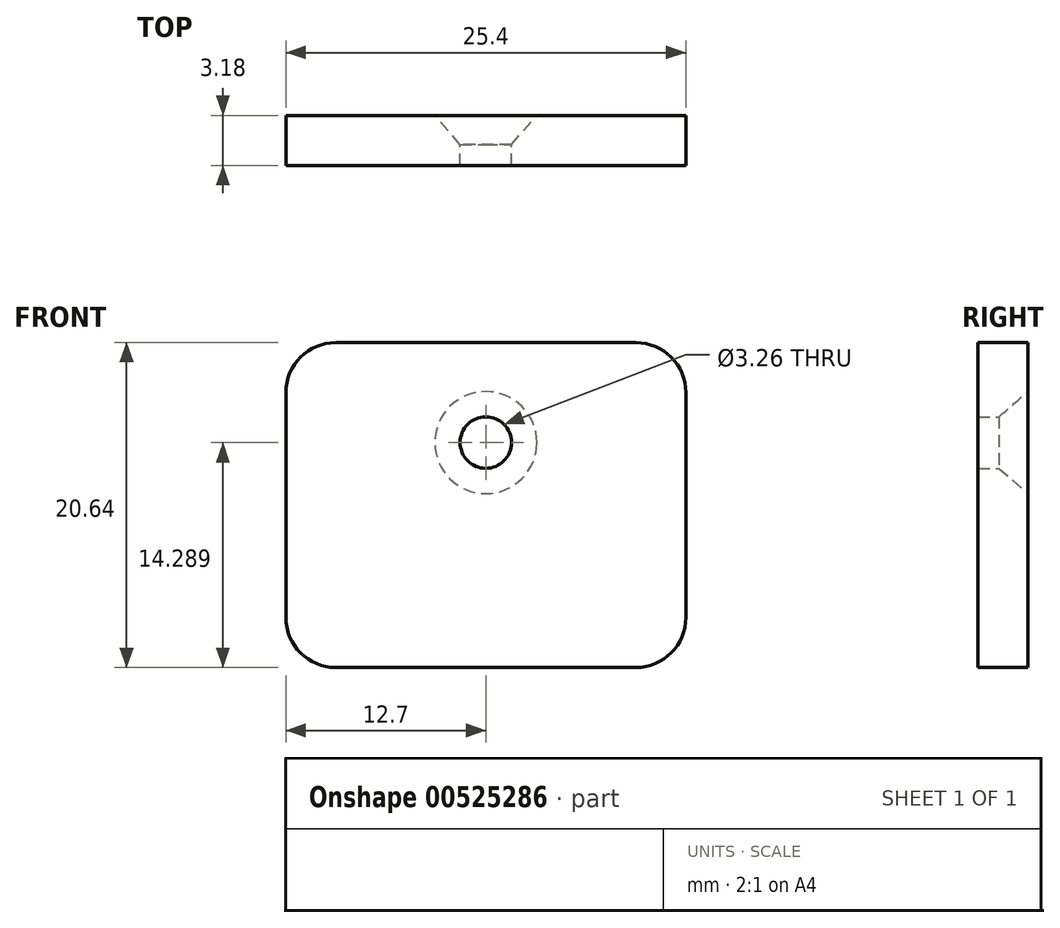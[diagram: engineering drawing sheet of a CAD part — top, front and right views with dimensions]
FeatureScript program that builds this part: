
annotation { "Feature Type Name" : "Feature", "Feature Type Description" : "" }
export const myFeature = defineFeature(function(context is Context, id is Id, definition is map)
    precondition{}
    {
        {
            var Q0;
            Q0=qCreatedBy(makeId("Front.planeOp"),FACE);
            var sketch = newSketch(context, id + "F0", { "sketchPlane" : qUnion([Q0])});
            skLineSegment(sketch, "E0.bottom", {"start": v(-12.7, 10.32) * mm, "end": v(12.7, 10.32) * mm});
            skLineSegment(sketch, "E0.top", {"start": v(-12.7, -10.32) * mm, "end": v(12.7, -10.32) * mm});
            skLineSegment(sketch, "E0.left", {"start": v(-12.7, 10.32) * mm, "end": v(-12.7, -10.32) * mm});
            skLineSegment(sketch, "E0.right", {"start": v(12.7, 10.32) * mm, "end": v(12.7, -10.32) * mm});
            skPoint(sketch, "E0.middle", {"position": v(0, 0) * mm});
            skLineSegment(sketch, "E1", {"start": v(21.09, 3.97) * mm, "end": v(-18.92, 3.97) * mm, "construction": true});
            skLineSegment(sketch, "E2", {"start": v(0, 0) * mm, "end": v(0, 20.1) * mm, "construction": true});
            skPoint(sketch, "E3", {"position": v(0, 3.97) * mm});
            skSolve(sketch);
        }
        {
            var Q0;
            Q0=makeQuery(id+"F0.imprint","IMPRINT",FACE,{"disambiguationData":[TD([[makeQuery(id+"F0.imprint","IMPRINT",EDGE,{"derivedFrom":sQuery(id+"F0.wireOp",EDGE,"E0.bottom")}),-1.0]])]});
            extrude(context, id + "F1", {"entities" : qUnion([Q0]), "depth" : 3.17 * mm, "offsetDistance" : 25.4 * mm});
        }
        {
            var Q0;
            Q0=makeQuery(id+"F1.opExtrude","CAP_FACE",FACE,{"disambiguationData":[OSD([sQuery(id+"F0.wireOp",EDGE,"E0.bottom"),sQuery(id+"F0.wireOp",EDGE,"E0.top"),sQuery(id+"F0.wireOp",EDGE,"E0.left"),sQuery(id+"F0.wireOp",EDGE,"E0.right")])],"isStart":true});
            var sketch = newSketch(context, id + "F2", { "sketchPlane" : qUnion([Q0])});
            skPoint(sketch, "E4", {"position": v(0, 3.97) * mm});
            skPoint(sketch, "E4.positionSnap0", {"position": v(0, 10.32) * mm});
            skSolve(sketch);
        }
        {
            var Q0;
            Q0=sQuery(id+"F2.wireOp",VERTEX,"E4");
            var Q1;
            Q1=makeQuery(id+"F1.opExtrude","SWEPT_BODY",BODY,{"disambiguationData":[OSD([sQuery(id+"F0.wireOp",EDGE,"E0.bottom"),sQuery(id+"F0.wireOp",EDGE,"E0.top"),sQuery(id+"F0.wireOp",EDGE,"E0.left"),sQuery(id+"F0.wireOp",EDGE,"E0.right")])]});
            hole(context, id + "F3", {"style" : HoleStyle.C_SINK, "endStyle" : HoleEndStyle.THROUGH, "standardTappedOrClearance" : lookupTablePath({ "standard" : "ANSI", "fit" : "Normal (ASME)", "size" : "#4", "type" : "Clearance" }), "standardBlindInLast" : lookupTablePath({ "fit" : "Free", "standard" : "ANSI", "size" : "#4", "type" : "Clearance" }), "holeDiameter" : 3.26 * mm, "cSinkDiameter" : 6.48 * mm, "cSinkAngle" : 82 * degree, "isTappedThrough" : true, "tappedDepth" : 12.7 * mm, "tapClearance" : 3, "locations" : qUnion([Q0]), "scope" : qUnion([Q1]), "majorDiameter" : 6.35 * mm});
        }
        {
            var Q0;
            Q0=makeQuery(id+"F1.opExtrude","SWEPT_EDGE",EDGE,{"disambiguationData":[OSD([sQuery(id+"F0.wireOp",EDGE,"E0.bottom"),sQuery(id+"F0.wireOp",EDGE,"E0.right")])]});
            var Q1;
            Q1=makeQuery(id+"F1.opExtrude","SWEPT_EDGE",EDGE,{"disambiguationData":[OSD([sQuery(id+"F0.wireOp",EDGE,"E0.bottom"),sQuery(id+"F0.wireOp",EDGE,"E0.left")])]});
            var Q2;
            Q2=makeQuery(id+"F1.opExtrude","SWEPT_EDGE",EDGE,{"disambiguationData":[OSD([sQuery(id+"F0.wireOp",EDGE,"E0.top"),sQuery(id+"F0.wireOp",EDGE,"E0.left")])]});
            var Q3;
            Q3=makeQuery(id+"F1.opExtrude","SWEPT_EDGE",EDGE,{"disambiguationData":[OSD([sQuery(id+"F0.wireOp",EDGE,"E0.top"),sQuery(id+"F0.wireOp",EDGE,"E0.right")])]});
            fillet(context, id + "F4", {"entities" : qUnion([Q0, Q1, Q2, Q3]), "radius" : 3.17 * mm, "tangentPropagation" : true, "allowEdgeOverflow" : false});
        }
    });
